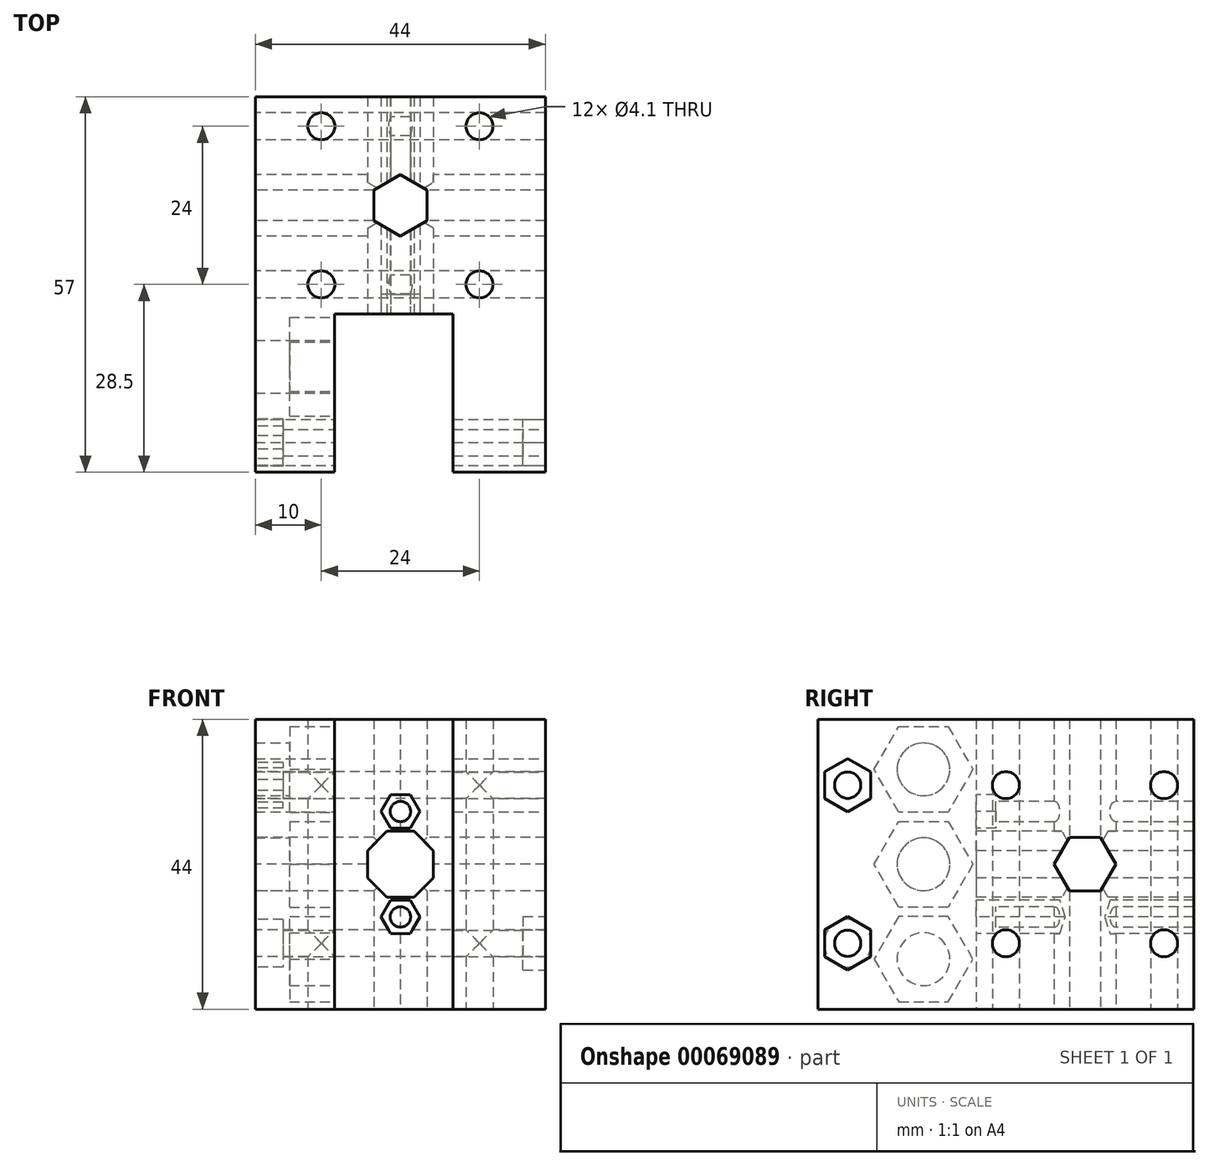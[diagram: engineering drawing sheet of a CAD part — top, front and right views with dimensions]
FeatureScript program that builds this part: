
annotation { "Feature Type Name" : "Feature", "Feature Type Description" : "" }
export const myFeature = defineFeature(function(context is Context, id is Id, definition is map)
    precondition{}
    {
        {
            var Q0;
            Q0=qCreatedBy(makeId("Top.planeOp"),FACE);
            var sketch = newSketch(context, id + "F0", { "sketchPlane" : qUnion([Q0])});
            skLineSegment(sketch, "E0.bottom", {"start": v(12, 12) * mm, "end": v(-12, 12) * mm, "construction": true});
            skLineSegment(sketch, "E0.top", {"start": v(12, -12) * mm, "end": v(-12, -12) * mm, "construction": true});
            skLineSegment(sketch, "E0.left", {"start": v(12, 12) * mm, "end": v(12, -12) * mm, "construction": true});
            skLineSegment(sketch, "E0.right", {"start": v(-12, 12) * mm, "end": v(-12, -12) * mm, "construction": true});
            skPoint(sketch, "E0.middle", {"position": v(0, 0) * mm});
            skCircle(sketch, "E1", {"center": v(-12, 12) * mm, "radius": 2.05 * mm});
            skCircle(sketch, "E2", {"center": v(12, 12) * mm, "radius": 2.05 * mm});
            skCircle(sketch, "E3", {"center": v(12, -12) * mm, "radius": 2.05 * mm});
            skCircle(sketch, "E4", {"center": v(-12, -12) * mm, "radius": 2.05 * mm});
            skLineSegment(sketch, "E5", {"start": v(-16.5, 16.5) * mm, "end": v(16.5, 16.5) * mm});
            skLineSegment(sketch, "E6", {"start": v(16.5, 16.5) * mm, "end": v(16.5, 16.5) * mm});
            skLineSegment(sketch, "E7", {"start": v(16.5, 16.5) * mm, "end": v(22, 16.5) * mm});
            skLineSegment(sketch, "E8", {"start": v(22, 16.5) * mm, "end": v(22, -32.5) * mm});
            skLineSegment(sketch, "E9", {"start": v(22, -32.5) * mm, "end": v(8, -32.5) * mm});
            skLineSegment(sketch, "E10", {"start": v(8, -32.5) * mm, "end": v(8, -16.5) * mm});
            skLineSegment(sketch, "E11", {"start": v(8, -16.5) * mm, "end": v(-10, -16.5) * mm});
            skLineSegment(sketch, "E12", {"start": v(-10, -16.5) * mm, "end": v(-10, -32.5) * mm});
            skLineSegment(sketch, "E13", {"start": v(-10, -32.5) * mm, "end": v(-22, -32.5) * mm});
            skLineSegment(sketch, "E14", {"start": v(-22, -32.5) * mm, "end": v(-22, 16.5) * mm});
            skLineSegment(sketch, "E15", {"start": v(-22, 16.5) * mm, "end": v(-16.5, 16.5) * mm});
            skLineSegment(sketch, "E16", {"start": v(-16.5, 16.5) * mm, "end": v(-16.5, 16.5) * mm});
            skLineSegment(sketch, "E17.bottom", {"start": v(8, -32.5) * mm, "end": v(-8, -32.5) * mm, "construction": true});
            skLineSegment(sketch, "E17.top", {"start": v(8, -16.5) * mm, "end": v(-8, -16.5) * mm, "construction": true});
            skLineSegment(sketch, "E17.left", {"start": v(8, -32.5) * mm, "end": v(8, -16.5) * mm, "construction": true});
            skLineSegment(sketch, "E17.right", {"start": v(-8, -32.5) * mm, "end": v(-8, -16.5) * mm, "construction": true});
            skPoint(sketch, "E18", {"position": v(0, -32.5) * mm});
            skLineSegment(sketch, "E19", {"start": v(0, -16.5) * mm, "end": v(0, 16.5) * mm, "construction": true});
            skSolve(sketch);
        }
        {
            var Q0;
            Q0=makeQuery(id+"F0.imprint","IMPRINT",FACE,{"disambiguationData":[TD([[makeQuery(id+"F0.imprint","IMPRINT",EDGE,{"derivedFrom":sQuery(id+"F0.wireOp",EDGE,"E1")}),-1.0]])]});
            extrude(context, id + "F1", {"entities" : qUnion([Q0]), "depth" : 44 * mm});
        }
        {
            var Q0;
            Q0=makeQuery(id+"F1.opExtrude","SWEPT_FACE",FACE,{"disambiguationData":[OSD([sQuery(id+"F0.wireOp",EDGE,"E12")])]});
            var sketch = newSketch(context, id + "F2", { "sketchPlane" : qUnion([Q0])});
            skLineSegment(sketch, "E20", {"start": v(-32.5, 22) * mm, "end": v(-16.5, 22) * mm, "construction": true});
            skCircle(sketch, "E21", {"center": v(-24.5, 22) * mm, "radius": 4 * mm});
            skCircle(sketch, "E22.cCircle", {"center": v(-24.5, 22) * mm, "radius": 6.5 * mm, "construction": true});
            skLineSegment(sketch, "E22.0", {"start": v(-20.75, 28.5) * mm, "end": v(-17, 22) * mm});
            skLineSegment(sketch, "E22.1", {"start": v(-17, 22) * mm, "end": v(-20.75, 15.5) * mm});
            skLineSegment(sketch, "E22.2", {"start": v(-20.75, 15.5) * mm, "end": v(-28.25, 15.5) * mm});
            skLineSegment(sketch, "E22.3", {"start": v(-28.25, 15.5) * mm, "end": v(-32, 22) * mm});
            skLineSegment(sketch, "E22.4", {"start": v(-32, 22) * mm, "end": v(-28.25, 28.5) * mm});
            skLineSegment(sketch, "E22.5", {"start": v(-28.25, 28.5) * mm, "end": v(-20.75, 28.5) * mm});
            skPoint(sketch, "E22.0.midPoint", {"position": v(-18.87, 25.25) * mm});
            skCircle(sketch, "E23", {"center": v(-24.5, 36.4) * mm, "radius": 4 * mm});
            skCircle(sketch, "E24.cCircle", {"center": v(-24.5, 36.4) * mm, "radius": 6.5 * mm, "construction": true});
            skLineSegment(sketch, "E24.0", {"start": v(-20.75, 42.9) * mm, "end": v(-17, 36.4) * mm});
            skLineSegment(sketch, "E24.1", {"start": v(-17, 36.4) * mm, "end": v(-20.75, 29.9) * mm});
            skLineSegment(sketch, "E24.2", {"start": v(-20.75, 29.9) * mm, "end": v(-28.25, 29.9) * mm});
            skLineSegment(sketch, "E24.3", {"start": v(-28.25, 29.9) * mm, "end": v(-32, 36.4) * mm});
            skLineSegment(sketch, "E24.4", {"start": v(-32, 36.4) * mm, "end": v(-28.25, 42.9) * mm});
            skLineSegment(sketch, "E24.5", {"start": v(-28.25, 42.9) * mm, "end": v(-20.75, 42.9) * mm});
            skPoint(sketch, "E24.0.midPoint", {"position": v(-18.87, 39.65) * mm});
            skLineSegment(sketch, "E25.MirrorCS", {"start": v(-32, 7.6) * mm, "end": v(-28.25, 1.1) * mm});
            skLineSegment(sketch, "E26.MirrorCS", {"start": v(-28.25, 14.1) * mm, "end": v(-32, 7.6) * mm});
            skLineSegment(sketch, "E27.MirrorCS", {"start": v(-20.75, 14.1) * mm, "end": v(-28.25, 14.1) * mm});
            skCircle(sketch, "E28.MirrorC", {"center": v(-24.5, 7.6) * mm, "radius": 4 * mm});
            skCircle(sketch, "E29.MirrorC", {"center": v(-24.5, 7.6) * mm, "radius": 6.5 * mm, "construction": true});
            skLineSegment(sketch, "E30.MirrorCS", {"start": v(-20.75, 1.1) * mm, "end": v(-17, 7.6) * mm});
            skLineSegment(sketch, "E31.MirrorCS", {"start": v(-28.25, 1.1) * mm, "end": v(-20.75, 1.1) * mm});
            skLineSegment(sketch, "E32.MirrorCS", {"start": v(-17, 7.6) * mm, "end": v(-20.75, 14.1) * mm});
            skPoint(sketch, "E33.MirrorP", {"position": v(-18.87, 4.35) * mm});
            skSolve(sketch);
        }
        {
            var Q0;
            Q0=makeQuery(id+"F2.imprint","IMPRINT",FACE,{"disambiguationData":[TD([[makeQuery(id+"F2.imprint","IMPRINT",EDGE,{"derivedFrom":sQuery(id+"F2.wireOp",EDGE,"E23")}),1.0]])]});
            var Q1;
            Q1=makeQuery(id+"F2.imprint","IMPRINT",FACE,{"disambiguationData":[TD([[makeQuery(id+"F2.imprint","IMPRINT",EDGE,{"derivedFrom":sQuery(id+"F2.wireOp",EDGE,"E21")}),1.0]])]});
            var Q2;
            Q2=makeQuery(id+"F2.imprint","IMPRINT",FACE,{"disambiguationData":[TD([[makeQuery(id+"F2.imprint","IMPRINT",EDGE,{"derivedFrom":sQuery(id+"F2.wireOp",EDGE,"E28.MirrorC")}),-1.0]])]});
            extrude(context, id + "F3", {"entities" : qUnion([Q0, Q1, Q2]), "operationType" : NewBodyOperationType.REMOVE, "endBound" : BoundingType.THROUGH_ALL, "oppositeDirection" : true, "depth" : 25 * mm});
        }
        {
            var Q0;
            Q0=makeQuery(id+"F2.imprint","IMPRINT",FACE,{"disambiguationData":[TD([[makeQuery(id+"F2.imprint","IMPRINT",EDGE,{"derivedFrom":sQuery(id+"F2.wireOp",EDGE,"E23")}),-1.0]])]});
            var Q1;
            Q1=makeQuery(id+"F2.imprint","IMPRINT",FACE,{"disambiguationData":[TD([[makeQuery(id+"F2.imprint","IMPRINT",EDGE,{"derivedFrom":sQuery(id+"F2.wireOp",EDGE,"E21")}),-1.0]])]});
            var Q2;
            Q2=makeQuery(id+"F2.imprint","IMPRINT",FACE,{"disambiguationData":[TD([[makeQuery(id+"F2.imprint","IMPRINT",EDGE,{"derivedFrom":sQuery(id+"F2.wireOp",EDGE,"E25.MirrorCS")}),1.0]])]});
            extrude(context, id + "F4", {"entities" : qUnion([Q0, Q1, Q2]), "operationType" : NewBodyOperationType.REMOVE, "oppositeDirection" : true, "depth" : 6.8 * mm});
        }
        {
            var Q0;
            Q0=makeQuery(id+"F1.opExtrude","SWEPT_FACE",FACE,{"disambiguationData":[OSD([sQuery(id+"F0.wireOp",EDGE,"E11")])]});
            var sketch = newSketch(context, id + "F5", { "sketchPlane" : qUnion([Q0])});
            skPoint(sketch, "E34.0", {"position": v(0, 0) * mm});
            skLineSegment(sketch, "E35", {"start": v(0, 0) * mm, "end": v(0, 44) * mm, "construction": true});
            skCircle(sketch, "E36.cCircle", {"center": v(0, 22) * mm, "radius": 5 * mm, "construction": true});
            skLineSegment(sketch, "E36.0", {"start": v(-2.07, 27) * mm, "end": v(2.07, 27) * mm});
            skLineSegment(sketch, "E36.1", {"start": v(2.07, 27) * mm, "end": v(5, 24.07) * mm});
            skLineSegment(sketch, "E36.2", {"start": v(5, 24.07) * mm, "end": v(5, 19.93) * mm});
            skLineSegment(sketch, "E36.3", {"start": v(5, 19.93) * mm, "end": v(2.07, 17) * mm});
            skLineSegment(sketch, "E36.4", {"start": v(2.07, 17) * mm, "end": v(-2.07, 17) * mm});
            skLineSegment(sketch, "E36.5", {"start": v(-2.07, 17) * mm, "end": v(-5, 19.93) * mm});
            skLineSegment(sketch, "E36.6", {"start": v(-5, 19.93) * mm, "end": v(-5, 24.07) * mm});
            skLineSegment(sketch, "E36.7", {"start": v(-5, 24.07) * mm, "end": v(-2.07, 27) * mm});
            skPoint(sketch, "E36.0.midPoint", {"position": v(0, 27) * mm});
            skSolve(sketch);
        }
        {
            var Q0;
            Q0 = qSketchRegion(id + "F5", true);
            extrude(context, id + "F6", {"entities" : qUnion([Q0]), "operationType" : NewBodyOperationType.REMOVE, "endBound" : BoundingType.THROUGH_ALL, "oppositeDirection" : true, "depth" : 25 * mm});
        }
        {
            var Q0;
            Q0=makeQuery(id+"F1.opExtrude","SWEPT_FACE",FACE,{"disambiguationData":[OSD([sQuery(id+"F0.wireOp",EDGE,"E14")])]});
            var sketch = newSketch(context, id + "F7", { "sketchPlane" : qUnion([Q0])});
            skLineSegment(sketch, "E37", {"start": v(0, 0) * mm, "end": v(0, 44) * mm, "construction": true});
            skLineSegment(sketch, "E38.bottom", {"start": v(-12, 34) * mm, "end": v(12, 34) * mm, "construction": true});
            skLineSegment(sketch, "E38.top", {"start": v(-12, 10) * mm, "end": v(12, 10) * mm, "construction": true});
            skLineSegment(sketch, "E38.left", {"start": v(-12, 34) * mm, "end": v(-12, 10) * mm, "construction": true});
            skLineSegment(sketch, "E38.right", {"start": v(12, 34) * mm, "end": v(12, 10) * mm, "construction": true});
            skPoint(sketch, "E38.middle", {"position": v(0, 22) * mm});
            skCircle(sketch, "E39", {"center": v(-12, 34) * mm, "radius": 2.05 * mm});
            skCircle(sketch, "E40", {"center": v(12, 34) * mm, "radius": 2.05 * mm});
            skCircle(sketch, "E41", {"center": v(12, 10) * mm, "radius": 2.05 * mm});
            skCircle(sketch, "E42", {"center": v(-12, 10) * mm, "radius": 2.05 * mm});
            skSolve(sketch);
        }
        {
            var Q0;
            Q0 = qSketchRegion(id + "F7", true);
            extrude(context, id + "F8", {"entities" : qUnion([Q0]), "operationType" : NewBodyOperationType.REMOVE, "endBound" : BoundingType.THROUGH_ALL, "oppositeDirection" : true, "depth" : 25 * mm});
        }
        {
            var Q0;
            Q0=makeQuery(id+"F1.opExtrude","SWEPT_FACE",FACE,{"disambiguationData":[OSD([sQuery(id+"F0.wireOp",EDGE,"E9")])]});
            var Q1;
            Q1=makeQuery(id+"F1.opExtrude","SWEPT_FACE",FACE,{"disambiguationData":[OSD([sQuery(id+"F0.wireOp",EDGE,"E13")])]});
            extrude(context, id + "F9", {"entities" : qUnion([Q0, Q1]), "operationType" : NewBodyOperationType.ADD, "depth" : 8 * mm});
        }
        {
            var Q0;
            {var subQ0=sQuery(id+"F0.wireOp",EDGE,"E8");Q0=makeQuery(id+"F9.boolean.opBoolean","MERGE",FACE,{"derivedFrom":[makeQuery(id+"F1.opExtrude","SWEPT_FACE",FACE,{"disambiguationData":[OSD([subQ0])]}),makeQuery(id+"F9.opExtrude","SWEPT_FACE",FACE,{"disambiguationData":[OSD([subQ0,sQuery(id+"F0.wireOp",EDGE,"E9")])]})]});}
            var sketch = newSketch(context, id + "F10", { "sketchPlane" : qUnion([Q0])});
            skLineSegment(sketch, "E43", {"start": v(-40.5, 22) * mm, "end": v(16.5, 22) * mm, "construction": true});
            skCircle(sketch, "E44", {"center": v(-36, 10) * mm, "radius": 2 * mm});
            skCircle(sketch, "E45.cCircle", {"center": v(-36, 10) * mm, "radius": 3.5 * mm, "construction": true});
            skLineSegment(sketch, "E45.0", {"start": v(-32.5, 12.02) * mm, "end": v(-32.5, 7.98) * mm});
            skLineSegment(sketch, "E45.1", {"start": v(-32.5, 7.98) * mm, "end": v(-36, 5.96) * mm});
            skLineSegment(sketch, "E45.2", {"start": v(-36, 5.96) * mm, "end": v(-39.5, 7.98) * mm});
            skLineSegment(sketch, "E45.3", {"start": v(-39.5, 7.98) * mm, "end": v(-39.5, 12.02) * mm});
            skLineSegment(sketch, "E45.4", {"start": v(-39.5, 12.02) * mm, "end": v(-36, 14.04) * mm});
            skLineSegment(sketch, "E45.5", {"start": v(-36, 14.04) * mm, "end": v(-32.5, 12.02) * mm});
            skPoint(sketch, "E45.0.midPoint", {"position": v(-32.5, 10) * mm});
            skLineSegment(sketch, "E46.0", {"start": v(-16.5, 44) * mm, "end": v(-16.5, 0) * mm, "construction": true});
            skLineSegment(sketch, "E47.MirrorCS", {"start": v(-32.5, 36.02) * mm, "end": v(-36, 38.04) * mm});
            skLineSegment(sketch, "E48.MirrorCS", {"start": v(-39.5, 31.98) * mm, "end": v(-36, 29.96) * mm});
            skLineSegment(sketch, "E49.MirrorCS", {"start": v(-36, 29.96) * mm, "end": v(-32.5, 31.98) * mm});
            skLineSegment(sketch, "E50.MirrorCS", {"start": v(-36, 38.04) * mm, "end": v(-39.5, 36.02) * mm});
            skLineSegment(sketch, "E51.MirrorCS", {"start": v(-32.5, 31.98) * mm, "end": v(-32.5, 36.02) * mm});
            skLineSegment(sketch, "E52.MirrorCS", {"start": v(-39.5, 36.02) * mm, "end": v(-39.5, 31.98) * mm});
            skCircle(sketch, "E53.MirrorC", {"center": v(-36, 34) * mm, "radius": 3.5 * mm, "construction": true});
            skCircle(sketch, "E54.MirrorC", {"center": v(-36, 34) * mm, "radius": 2 * mm});
            skPoint(sketch, "E55.MirrorP", {"position": v(-32.5, 34) * mm});
            skSolve(sketch);
        }
        {
            var Q0;
            Q0=makeQuery(id+"F10.imprint","IMPRINT",FACE,{"disambiguationData":[TD([[makeQuery(id+"F10.imprint","IMPRINT",EDGE,{"derivedFrom":sQuery(id+"F10.wireOp",EDGE,"E44")}),1.0]])]});
            var Q1;
            Q1=makeQuery(id+"F10.imprint","IMPRINT",FACE,{"disambiguationData":[TD([[makeQuery(id+"F10.imprint","IMPRINT",EDGE,{"derivedFrom":sQuery(id+"F10.wireOp",EDGE,"E54.MirrorC")}),-1.0]])]});
            extrude(context, id + "F11", {"entities" : qUnion([Q0, Q1]), "operationType" : NewBodyOperationType.REMOVE, "endBound" : BoundingType.THROUGH_ALL, "oppositeDirection" : true, "depth" : 25 * mm});
        }
        {
            var Q0;
            Q0=makeQuery(id+"F10.imprint","IMPRINT",FACE,{"disambiguationData":[TD([[makeQuery(id+"F10.imprint","IMPRINT",EDGE,{"derivedFrom":sQuery(id+"F10.wireOp",EDGE,"E44")}),-1.0]])]});
            var Q1;
            Q1=makeQuery(id+"F10.imprint","IMPRINT",FACE,{"disambiguationData":[TD([[makeQuery(id+"F10.imprint","IMPRINT",EDGE,{"derivedFrom":sQuery(id+"F10.wireOp",EDGE,"E47.MirrorCS")}),1.0]])]});
            extrude(context, id + "F12", {"entities" : qUnion([Q0, Q1]), "operationType" : NewBodyOperationType.REMOVE, "oppositeDirection" : true, "depth" : 3.4 * mm});
        }
        {
            var Q0;
            {var subQ0=sQuery(id+"F0.wireOp",EDGE,"E14");Q0=makeQuery(id+"F9.boolean.opBoolean","MERGE",FACE,{"derivedFrom":[makeQuery(id+"F1.opExtrude","SWEPT_FACE",FACE,{"disambiguationData":[OSD([subQ0])]}),makeQuery(id+"F9.opExtrude","SWEPT_FACE",FACE,{"disambiguationData":[OSD([sQuery(id+"F0.wireOp",EDGE,"E13"),subQ0])]})]});}
            var sketch = newSketch(context, id + "F13", { "sketchPlane" : qUnion([Q0])});
            skCircle(sketch, "E56", {"center": v(36, 10) * mm, "radius": 3.6 * mm});
            skCircle(sketch, "E57", {"center": v(36, 34) * mm, "radius": 3.6 * mm});
            skSolve(sketch);
        }
        {
            var Q0;
            Q0 = qSketchRegion(id + "F13", true);
            extrude(context, id + "F14", {"entities" : qUnion([Q0]), "operationType" : NewBodyOperationType.REMOVE, "oppositeDirection" : true, "depth" : 4.2 * mm});
        }
        {
            var Q0;
            {var subQ0=sQuery(id+"F0.wireOp",EDGE,"E13");var subQ1=sQuery(id+"F0.wireOp",EDGE,"E9");Q0=makeQuery(id+"F9.boolean.opBoolean","MERGE",FACE,{"derivedFrom":[makeQuery(id+"F1.opExtrude","CAP_FACE",FACE,{"disambiguationData":[OSD([sQuery(id+"F0.wireOp",EDGE,"E1"),sQuery(id+"F0.wireOp",EDGE,"E2"),sQuery(id+"F0.wireOp",EDGE,"E3"),sQuery(id+"F0.wireOp",EDGE,"E4"),sQuery(id+"F0.wireOp",EDGE,"E5"),sQuery(id+"F0.wireOp",EDGE,"E7"),sQuery(id+"F0.wireOp",EDGE,"E8"),subQ1,sQuery(id+"F0.wireOp",EDGE,"E10"),sQuery(id+"F0.wireOp",EDGE,"E11"),sQuery(id+"F0.wireOp",EDGE,"E12"),subQ0,sQuery(id+"F0.wireOp",EDGE,"E14"),sQuery(id+"F0.wireOp",EDGE,"E15")])],"isStart":true}),makeQuery(id+"F9.opExtrude","SWEPT_FACE",FACE,{"disambiguationData":[OSD([subQ1]),TDD([makeQuery(id+"F1.opExtrude","CAP_EDGE",EDGE,{"disambiguationData":[OSD([subQ1])],"isStart":true})])]}),makeQuery(id+"F9.opExtrude","SWEPT_FACE",FACE,{"disambiguationData":[OSD([subQ0]),TDD([makeQuery(id+"F1.opExtrude","CAP_EDGE",EDGE,{"disambiguationData":[OSD([subQ0])],"isStart":true})])]})]});}
            var sketch = newSketch(context, id + "F15", { "sketchPlane" : qUnion([Q0])});
            skCircle(sketch, "E58.cCircle", {"center": v(0, 0) * mm, "radius": 4.05 * mm, "construction": true});
            skLineSegment(sketch, "E58.0", {"start": v(0, -4.68) * mm, "end": v(-4.05, -2.34) * mm});
            skLineSegment(sketch, "E58.1", {"start": v(-4.05, -2.34) * mm, "end": v(-4.05, 2.34) * mm});
            skLineSegment(sketch, "E58.2", {"start": v(-4.05, 2.34) * mm, "end": v(0, 4.68) * mm});
            skLineSegment(sketch, "E58.3", {"start": v(0, 4.68) * mm, "end": v(4.05, 2.34) * mm});
            skLineSegment(sketch, "E58.4", {"start": v(4.05, 2.34) * mm, "end": v(4.05, -2.34) * mm});
            skLineSegment(sketch, "E58.5", {"start": v(4.05, -2.34) * mm, "end": v(0, -4.68) * mm});
            skPoint(sketch, "E58.0.midPoint", {"position": v(-2.03, -3.5) * mm});
            skSolve(sketch);
        }
        {
            var Q0;
            Q0 = qSketchRegion(id + "F15", true);
            extrude(context, id + "F16", {"entities" : qUnion([Q0]), "operationType" : NewBodyOperationType.REMOVE, "endBound" : BoundingType.THROUGH_ALL, "oppositeDirection" : true, "depth" : 25 * mm});
        }
        {
            var Q0;
            {var subQ0=sQuery(id+"F0.wireOp",EDGE,"E14");Q0=makeQuery(id+"F9.boolean.opBoolean","MERGE",FACE,{"derivedFrom":[makeQuery(id+"F1.opExtrude","SWEPT_FACE",FACE,{"disambiguationData":[OSD([subQ0])]}),makeQuery(id+"F9.opExtrude","SWEPT_FACE",FACE,{"disambiguationData":[OSD([sQuery(id+"F0.wireOp",EDGE,"E13"),subQ0])]})]});}
            var sketch = newSketch(context, id + "F17", { "sketchPlane" : qUnion([Q0])});
            skCircle(sketch, "E59.cCircle", {"center": v(0, 22) * mm, "radius": 4.05 * mm, "construction": true});
            skLineSegment(sketch, "E59.0", {"start": v(2.34, 17.95) * mm, "end": v(-2.34, 17.95) * mm});
            skLineSegment(sketch, "E59.1", {"start": v(-2.34, 17.95) * mm, "end": v(-4.68, 22) * mm});
            skLineSegment(sketch, "E59.2", {"start": v(-4.68, 22) * mm, "end": v(-2.34, 26.05) * mm});
            skLineSegment(sketch, "E59.3", {"start": v(-2.34, 26.05) * mm, "end": v(2.34, 26.05) * mm});
            skLineSegment(sketch, "E59.4", {"start": v(2.34, 26.05) * mm, "end": v(4.68, 22) * mm});
            skLineSegment(sketch, "E59.5", {"start": v(4.68, 22) * mm, "end": v(2.34, 17.95) * mm});
            skPoint(sketch, "E59.0.midPoint", {"position": v(0, 17.95) * mm});
            skLineSegment(sketch, "E60", {"start": v(0, 0) * mm, "end": v(0, 44) * mm, "construction": true});
            skSolve(sketch);
        }
        {
            var Q0;
            Q0 = qSketchRegion(id + "F17", true);
            extrude(context, id + "F18", {"entities" : qUnion([Q0]), "operationType" : NewBodyOperationType.REMOVE, "endBound" : BoundingType.THROUGH_ALL, "oppositeDirection" : true, "depth" : 25 * mm});
        }
        {
            var Q0;
            Q0=makeQuery(id+"F1.opExtrude","SWEPT_FACE",FACE,{"disambiguationData":[OSD([sQuery(id+"F0.wireOp",EDGE,"E11")])]});
            var sketch = newSketch(context, id + "F19", { "sketchPlane" : qUnion([Q0])});
            skLineSegment(sketch, "E61", {"start": v(-10, 22) * mm, "end": v(8, 22) * mm, "construction": true});
            skCircle(sketch, "E62", {"center": v(0, 30) * mm, "radius": 1.55 * mm});
            skCircle(sketch, "E63.cCircle", {"center": v(0, 30) * mm, "radius": 2.55 * mm, "construction": true});
            skLineSegment(sketch, "E63.0", {"start": v(1.47, 32.55) * mm, "end": v(-1.47, 32.55) * mm});
            skLineSegment(sketch, "E63.1", {"start": v(2.94, 30) * mm, "end": v(1.47, 32.55) * mm});
            skLineSegment(sketch, "E63.2", {"start": v(1.47, 27.45) * mm, "end": v(2.94, 30) * mm});
            skLineSegment(sketch, "E63.3", {"start": v(-1.47, 27.45) * mm, "end": v(1.47, 27.45) * mm});
            skLineSegment(sketch, "E63.4", {"start": v(-2.94, 30) * mm, "end": v(-1.47, 27.45) * mm});
            skLineSegment(sketch, "E63.5", {"start": v(-1.47, 32.55) * mm, "end": v(-2.94, 30) * mm});
            skPoint(sketch, "E63.0.midPoint", {"position": v(0, 32.55) * mm});
            skCircle(sketch, "E64.MirrorC", {"center": v(0, 14) * mm, "radius": 1.55 * mm});
            skLineSegment(sketch, "E65.MirrorCS", {"start": v(-2.94, 14) * mm, "end": v(-1.47, 16.55) * mm});
            skLineSegment(sketch, "E66.MirrorCS", {"start": v(1.47, 16.55) * mm, "end": v(2.94, 14) * mm});
            skLineSegment(sketch, "E67.MirrorCS", {"start": v(2.94, 14) * mm, "end": v(1.47, 11.45) * mm});
            skCircle(sketch, "E68.MirrorC", {"center": v(0, 14) * mm, "radius": 2.55 * mm, "construction": true});
            skLineSegment(sketch, "E69.MirrorCS", {"start": v(1.47, 11.45) * mm, "end": v(-1.47, 11.45) * mm});
            skLineSegment(sketch, "E70.MirrorCS", {"start": v(-1.47, 16.55) * mm, "end": v(1.47, 16.55) * mm});
            skLineSegment(sketch, "E71.MirrorCS", {"start": v(-1.47, 11.45) * mm, "end": v(-2.94, 14) * mm});
            skSolve(sketch);
        }
        {
            var Q0;
            Q0=makeQuery(id+"F19.imprint","IMPRINT",FACE,{"disambiguationData":[TD([[makeQuery(id+"F19.imprint","IMPRINT",EDGE,{"derivedFrom":sQuery(id+"F19.wireOp",EDGE,"E62")}),1.0]])]});
            var Q1;
            Q1=makeQuery(id+"F19.imprint","IMPRINT",FACE,{"disambiguationData":[TD([[makeQuery(id+"F19.imprint","IMPRINT",EDGE,{"derivedFrom":sQuery(id+"F19.wireOp",EDGE,"E64.MirrorC")}),-1.0]])]});
            extrude(context, id + "F20", {"entities" : qUnion([Q0, Q1]), "operationType" : NewBodyOperationType.REMOVE, "endBound" : BoundingType.THROUGH_ALL, "oppositeDirection" : true, "depth" : 25 * mm});
        }
        {
            var Q0;
            Q0=makeQuery(id+"F19.imprint","IMPRINT",FACE,{"disambiguationData":[TD([[makeQuery(id+"F19.imprint","IMPRINT",EDGE,{"derivedFrom":sQuery(id+"F19.wireOp",EDGE,"E62")}),-1.0]])]});
            var Q1;
            Q1=makeQuery(id+"F19.imprint","IMPRINT",FACE,{"disambiguationData":[TD([[makeQuery(id+"F19.imprint","IMPRINT",EDGE,{"derivedFrom":sQuery(id+"F19.wireOp",EDGE,"E64.MirrorC")}),1.0]])]});
            extrude(context, id + "F21", {"entities" : qUnion([Q0, Q1]), "operationType" : NewBodyOperationType.REMOVE, "oppositeDirection" : true, "depth" : 3 * mm});
        }
    });
